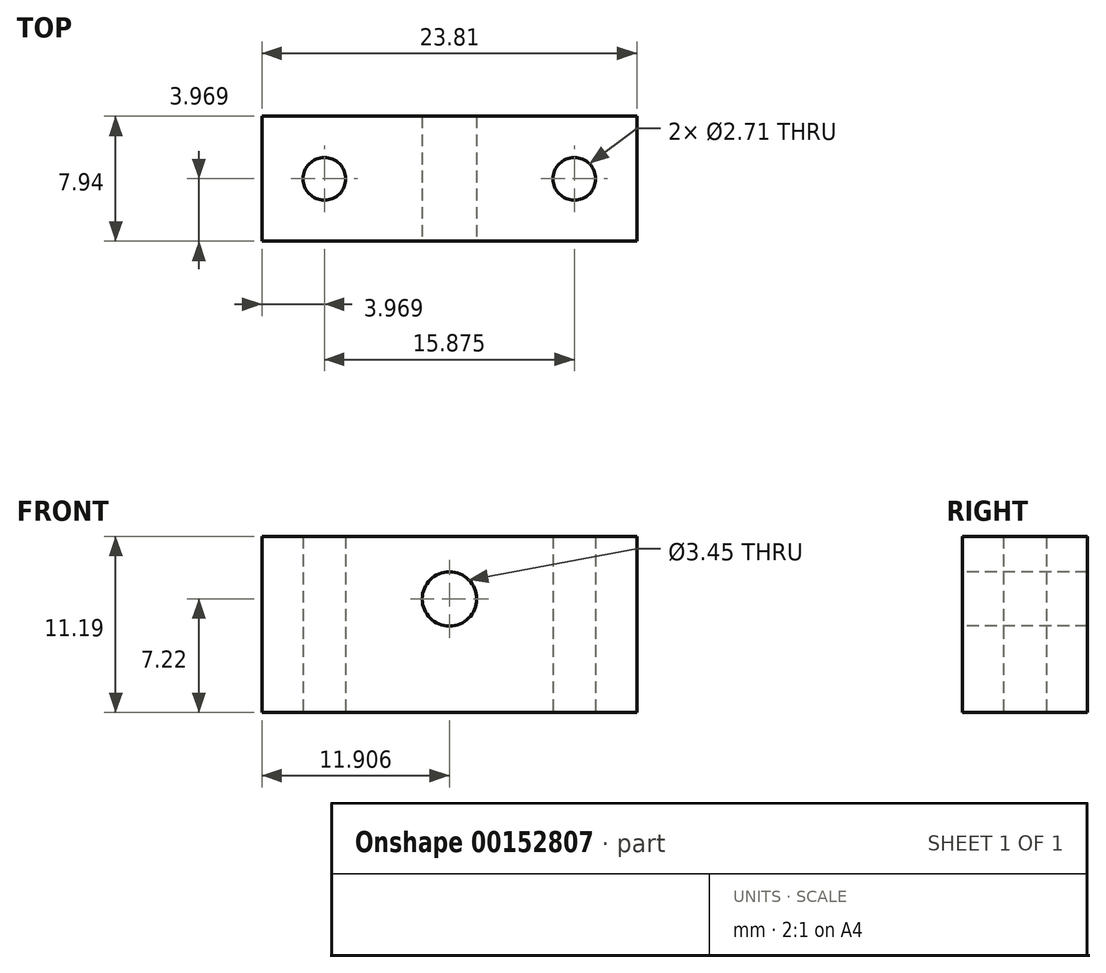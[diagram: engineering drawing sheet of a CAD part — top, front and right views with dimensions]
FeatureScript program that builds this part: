
annotation { "Feature Type Name" : "Feature", "Feature Type Description" : "" }
export const myFeature = defineFeature(function(context is Context, id is Id, definition is map)
    precondition{}
    {
        {
            var Q0;
            Q0=qCreatedBy(makeId("Top.planeOp"),FACE);
            var sketch = newSketch(context, id + "F0", { "sketchPlane" : qUnion([Q0])});
            skLineSegment(sketch, "E0.bottom", {"start": v(0, 0) * mm, "end": v(23.81, 0) * mm});
            skLineSegment(sketch, "E0.top", {"start": v(0, 7.94) * mm, "end": v(23.81, 7.94) * mm});
            skLineSegment(sketch, "E0.left", {"start": v(0, 0) * mm, "end": v(0, 7.94) * mm});
            skLineSegment(sketch, "E0.right", {"start": v(23.81, 0) * mm, "end": v(23.81, 7.94) * mm});
            skLineSegment(sketch, "E1", {"start": v(0, 3.97) * mm, "end": v(3.97, 3.97) * mm, "construction": true});
            skLineSegment(sketch, "E2", {"start": v(23.81, 3.97) * mm, "end": v(19.84, 3.97) * mm, "construction": true});
            skLineSegment(sketch, "E3", {"start": v(3.97, 3.97) * mm, "end": v(3.97, 7.94) * mm, "construction": true});
            skCircle(sketch, "E4", {"center": v(3.97, 3.97) * mm, "radius": 1.35 * mm});
            skCircle(sketch, "E5", {"center": v(19.84, 3.97) * mm, "radius": 1.35 * mm});
            skSolve(sketch);
        }
        {
            var Q0;
            Q0=qSketchRegion(id+"F0",true);
            extrude(context, id + "F1", {"entities" : qUnion([Q0]), "depth" : 11.2 * mm});
        }
        {
            var Q0;
            Q0=makeQuery(id+"F1.opExtrude","SWEPT_FACE",FACE,{"disambiguationData":[OSD([sQuery(id+"F0.wireOp",EDGE,"E0.bottom")])]});
            var sketch = newSketch(context, id + "F2", { "sketchPlane" : qUnion([Q0])});
            skLineSegment(sketch, "E6", {"start": v(11.9, 0) * mm, "end": v(11.9, 7.22) * mm, "construction": true});
            skCircle(sketch, "E7", {"center": v(11.9, 7.22) * mm, "radius": 1.73 * mm});
            skSolve(sketch);
        }
        {
            var Q0;
            Q0=qSketchRegion(id+"F2",true);
            var Q1;
            Q1=makeQuery(id+"F1.opExtrude","SWEPT_FACE",FACE,{"disambiguationData":[OSD([sQuery(id+"F0.wireOp",EDGE,"E0.top")])]});
            extrude(context, id + "F3", {"entities" : qUnion([Q0]), "operationType" : NewBodyOperationType.REMOVE, "endBound" : BoundingType.UP_TO_SURFACE, "oppositeDirection" : true, "endBoundEntityFace" : qUnion([Q1]), "depth" : 25.4 * mm});
        }
    });
